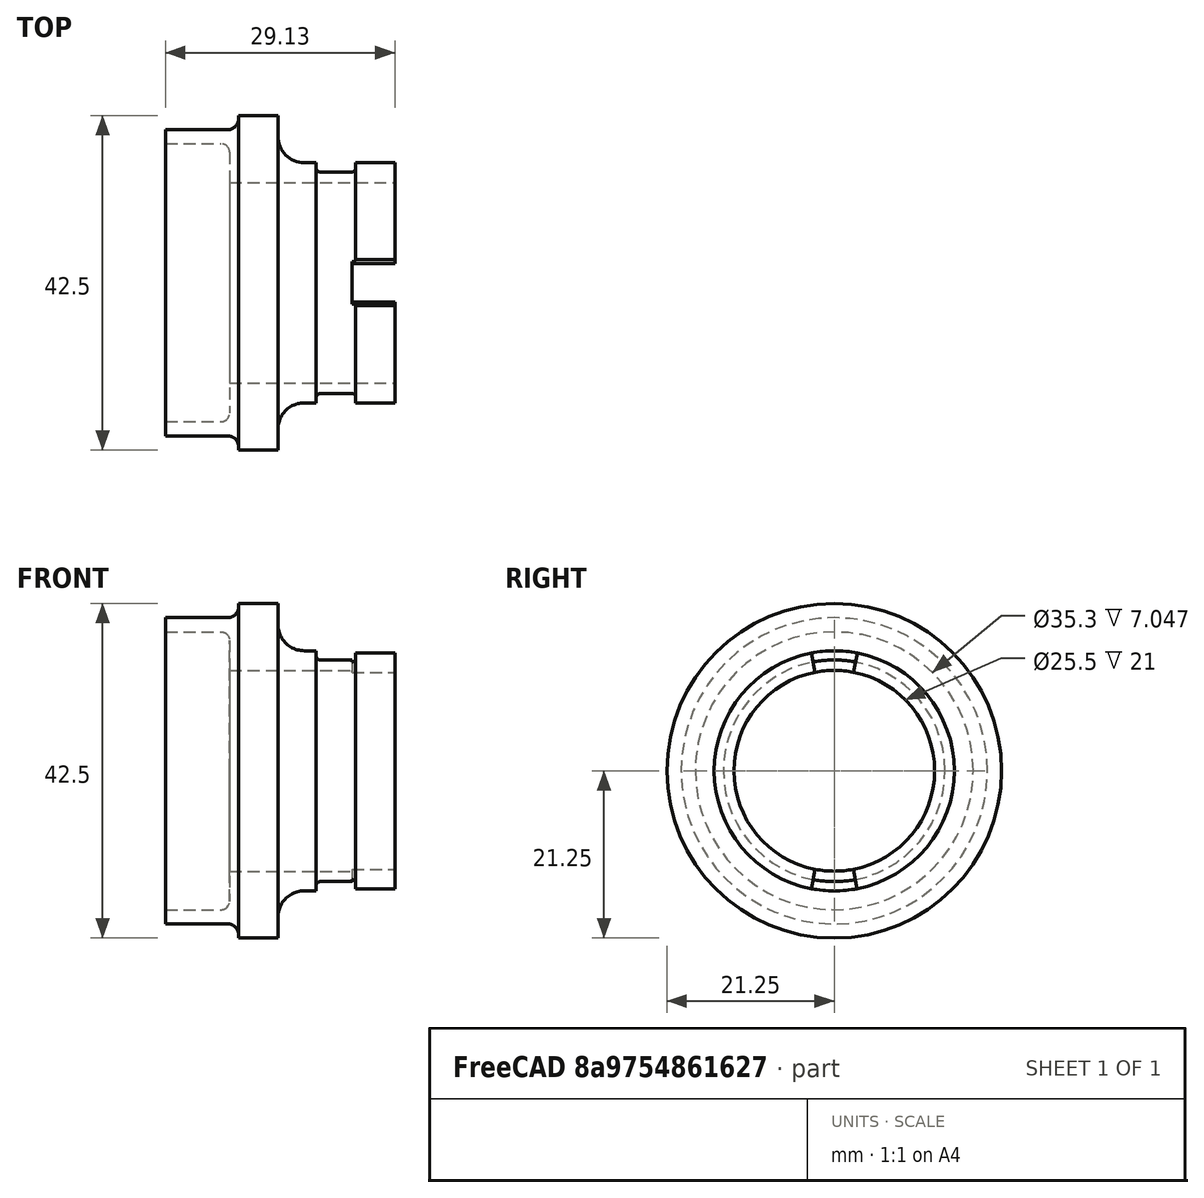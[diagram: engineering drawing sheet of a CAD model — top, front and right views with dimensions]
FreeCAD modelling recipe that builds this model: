
FCSTD DOCUMENT  (FreeCAD 0.18R16117 (Git))
Label: Adaptateur aspirateur et scie table
License: All rights reserved
LicenseURL: http://en.wikipedia.org/wiki/All_rights_reserved
objects: TechDraw::DrawViewDimension×9, Drawing::FeatureViewPart×5, TechDraw::DrawViewPart×5, Sketcher::SketchObject×4, PartDesign::Pocket×2, PartDesign::Revolution×1, PartDesign::Body×1, Drawing::FeaturePage×1, TechDraw::DrawSVGTemplate×1, TechDraw::DrawPage×1
note: 11 computed .brp shape members not serialized (recipe doc carries the construction recipe); baked Part::Feature solids carry a one-line shape summary decoded from their .brp

FEATURE [Sketcher::SketchObject] Sketch
  MapMode = 5
  Support = -> [XY_Plane]
  sketch-geometry (19):
    g0: LineSegment StartX=11.8162 StartY=18.5951 StartZ=0 EndX=11.8162 EndY=21.25 EndZ=0
    g1: LineSegment StartX=11.8162 StartY=21.25 StartZ=0 EndX=6.81623 EndY=21.25 EndZ=0
    g2: LineSegment StartX=6.81623 StartY=21.25 StartZ=0 EndX=6.81623 EndY=20.845 EndZ=0
    g3: LineSegment StartX=5.4212 StartY=19.45 StartZ=0 EndX=-2.45777 EndY=19.45 EndZ=0
    g4: LineSegment StartX=-2.45777 StartY=19.45 StartZ=0 EndX=-2.45777 EndY=17.65 EndZ=0
    g5: LineSegment StartX=-2.45777 StartY=17.65 StartZ=0 EndX=4.58894 EndY=17.65 EndZ=0
    g6: LineSegment StartX=5.67363 StartY=16.5653 StartZ=0 EndX=5.67363 EndY=12.75 EndZ=0
    g7: LineSegment StartX=5.67363 StartY=12.75 StartZ=0 EndX=26.6736 EndY=12.75 EndZ=0
    g8: LineSegment StartX=26.6736 StartY=12.75 StartZ=0 EndX=26.6736 EndY=15.25 EndZ=0
    g9: ArcOfCircle CenterX=4.58894 CenterY=16.5653 CenterZ=0 NormalX=0 NormalY=0 NormalZ=1 AngleXU=0 Radius=1.08469 StartAngle=-9e-16 EndAngle=1.5708
    g10: ArcOfCircle CenterX=5.4212 CenterY=20.845 CenterZ=0 NormalX=0 NormalY=0 NormalZ=1 AngleXU=0 Radius=1.39502 StartAngle=4.71239 EndAngle=6.28319
    g11: ArcOfCircle CenterX=15.1613 CenterY=18.5951 CenterZ=0 NormalX=0 NormalY=0 NormalZ=1 AngleXU=0 Radius=3.34505 StartAngle=3.14159 EndAngle=4.71239
    g12: LineSegment StartX=15.1613 StartY=15.25 StartZ=0 EndX=16.6736 EndY=15.25 EndZ=0
    g13: LineSegment StartX=16.6736 StartY=15.25 StartZ=0 EndX=16.6736 EndY=14.5875 EndZ=0
    g14: LineSegment StartX=17.1846 StartY=14.0765 StartZ=0 EndX=21.204 EndY=14.0765 EndZ=0
    g15: LineSegment StartX=21.6736 StartY=14.5461 StartZ=0 EndX=21.6736 EndY=15.25 EndZ=0
    g16: LineSegment StartX=21.6736 StartY=15.25 StartZ=0 EndX=26.6736 EndY=15.25 EndZ=0
    g17: ArcOfCircle CenterX=17.1846 CenterY=14.5875 CenterZ=0 NormalX=0 NormalY=0 NormalZ=1 AngleXU=0 Radius=0.510984 StartAngle=3.14159 EndAngle=4.71239
    g18: ArcOfCircle CenterX=21.204 CenterY=14.5461 CenterZ=0 NormalX=0 NormalY=0 NormalZ=1 AngleXU=0 Radius=0.469602 StartAngle=4.71239 EndAngle=6.28319
  constraints (39):
    c: Coincident(g0,g1)
    c: Coincident(g1,g2)
    c: Coincident(g3,g4)
    c: Coincident(g4,g5)
    c: Coincident(g6,g7)
    c: Coincident(g7,g8)
    c: Horizontal(g7)
    c: Horizontal(g5)
    c: Horizontal(g3)
    c: Horizontal(g1)
    c: Vertical(g4)
    c: Vertical(g2)
    c: Vertical(g6)
    c: Vertical(g8)
    c: Vertical(g0)
    c: Distance(g7,g-1) = 12.75  'Rayon intérieur côté scie'
    c: DistanceY(g8,g8) = 2.5
    c: DistanceX(g1,g1) = 5
    c: DistanceY(g-1,g4) = 17.65
    c: DistanceX(g7,g7) = 21
    c: Tangent(g5,g9) = 1.5708
    c: Tangent(g6,g9) = 1.5708
    c: Tangent(g3,g10) = 1.5708
    c: Tangent(g2,g10) = 1.5708
    c: Tangent(g0,g11) = 1.5708
    c: DistanceY(g4,g4) = 1.8
    c: Coincident(g12,g13)
    c: Coincident(g15,g16)
    c: Coincident(g16,g8)
    c: Horizontal(g16)
    c: Horizontal(g12)
    c: Horizontal(g14)
    c: Vertical(g13)
    c: Vertical(g15)
    c: DistanceX(g16,g16) = 5
    c: Tangent(g14,g17) = -1.5708
    c: Tangent(g13,g17) = -1.5708
    c: Tangent(g15,g18) = -1.5708
    c: Tangent(g14,g18) = -1.5708
FEATURE [PartDesign::Revolution] Revolution
  Angle = 360
  Axis = (1,0,0)
  Base = (0,0,0)
  Profile = -> Sketch
  ReferenceAxis = -> Sketch [H_Axis]
FEATURE [Sketcher::SketchObject] Sketch001
  MapMode = 5
  Placement = pos=(26.6736,0,0) rot=(0.57735,0.57735,0.57735;2.0944rad)
  Support = -> [Revolution]
  sketch-geometry (3):
    g0: LineSegment StartX=0 StartY=0 StartZ=0 EndX=-3 EndY=-15.4941 EndZ=0
    g1: LineSegment StartX=-3 StartY=-15.4941 StartZ=0 EndX=3 EndY=-15.4941 EndZ=0
    g2: LineSegment StartX=3 StartY=-15.4941 StartZ=0 EndX=0 EndY=0 EndZ=0
  constraints (7):
    c: Coincident(g0,g1)
    c: Coincident(g1,g2)
    c: Coincident(g2,g0)
    c: Coincident(g-1,g0)
    c: Perpendicular(g-2,g1)
    c: DistanceX(g-1,g1) = 3
    c: DistanceX(g-2,g0) = -3
FEATURE [PartDesign::Pocket] Pocket
  BaseFeature = -> Revolution
  Length = 5.45
  Length2 = 100
  Profile = -> Sketch001
  Type = 0
FEATURE [Sketcher::SketchObject] CopySketch002
  Placement = pos=(26.6736,0,0) rot=(0.57735,0.57735,0.57735;2.0944rad)
  sketch-geometry (3):
    g0: LineSegment StartX=0 StartY=0 StartZ=0 EndX=-3 EndY=15.3419 EndZ=0
    g1: LineSegment StartX=-3 StartY=15.3419 StartZ=0 EndX=3 EndY=15.3419 EndZ=0
    g2: LineSegment StartX=3 StartY=15.3419 StartZ=0 EndX=0 EndY=0 EndZ=0
  constraints (7):
    c: Coincident(g0,g1)
    c: Coincident(g1,g2)
    c: Coincident(g2,g0)
    c: Coincident(g-1,g0)
    c: Perpendicular(g-2,g1)
    c: DistanceX(g-1,g1) = 3
    c: DistanceX(g-2,g0) = -3
FEATURE [PartDesign::Pocket] Pocket001  label="Adaptateur"
  BaseFeature = -> Pocket
  Length = 5.45
  Length2 = 100
  Profile = -> CopySketch002
  Type = 0
FEATURE [PartDesign::Body] Body
  Group = -> [Sketch,Revolution,Sketch001,Pocket,Pocket001]
  Origin = -> Origin
  Tip = -> Pocket001
FEATURE [Sketcher::SketchObject] Sketch002
  MapMode = 5
  Placement = pos=(26.6736,0,0) rot=(0.57735,0.57735,0.57735;2.0944rad)
  Support = -> [Revolution]
  sketch-geometry (3):
    g0: LineSegment StartX=0 StartY=0 StartZ=0 EndX=-3 EndY=15.3419 EndZ=0
    g1: LineSegment StartX=-3 StartY=15.3419 StartZ=0 EndX=3 EndY=15.3419 EndZ=0
    g2: LineSegment StartX=3 StartY=15.3419 StartZ=0 EndX=0 EndY=0 EndZ=0
  constraints (7):
    c: Coincident(g0,g1)
    c: Coincident(g1,g2)
    c: Coincident(g2,g0)
    c: Coincident(g-1,g0)
    c: Perpendicular(g-2,g1)
    c: DistanceX(g-1,g1) = 3
    c: DistanceX(g-2,g0) = -3
FEATURE [Drawing::FeatureViewPart] Ortho  label="Cote scie"
  Direction = (1,0,0)
  HiddenWidth = 0.15
  LineWidth = 0.35
  Rotation = -90
  Scale = 1.5
  ShowHiddenLines = false
  ShowSmoothLines = false
  Source = -> Pocket001
  Tolerance = 0.05
  ViewResult = <g id="Ortho_0_0"\n   transform="rotate(-90,170,70) translate(170,70) scale(1.5,1.5)"\n  >\n<g   fill="none"\n   stroke="rgb(0, 0, 0)"\n   stroke-linecap="butt"\n   stroke-linejoin="miter"\n   stroke-width="0.233333"\n   transform="scale(1,-1)"\n  >\n<circle cx ="0" cy ="0" r ="21.25" /><path d="M14.9665 -2.9266 A15.25 15.25 0 0 1 14.9665 2.9266" /><path d="M-14.9719 2.8989 A15.25 15.25 0 0 1 -14.9719 -2.8989" /><path d="M13.8153,2.70148 C14.164,0.922951 14.164,-0.922951 13.8153,-2.70148 " /><path d="M-13.8203,-2.67591 C-14.1623,-0.913787 -14.1623,0.913787 -13.8203,2.67591 " /><path id= "6" d=" M 14.9665 -2.9266 L 12.513 -2.44683 " />\n<path d="M12.513 -2.44683 A12.75 12.75 0 0 1 12.513 2.44683" /><path id= "8" d=" M 12.513 2.44683 L 14.9665 2.9266 " />\n<path id= "9" d=" M -12.5175 2.42367 L -14.9719 2.8989 " />\n<path d="M-12.5175 2.42367 A12.75 12.75 0 0 1 -12.5175 -2.42367" /><path id= "11" d=" M -14.9719 -2.8989 L -12.5175 -2.42367 " />\n<path d="M-14.9719 -2.8989 A15.25 15.25 0 0 1 -3.73517e-15 -15.25" /><path d="M0 -15.25 A15.25 15.25 0 0 1 14.9665 -2.9266" /><path d="M0 -12.75 A12.75 12.75 0 0 1 12.513 -2.44683" /><path d="M-12.5175 -2.42367 A12.75 12.75 0 0 1 -3.12285e-15 -12.75" /><path d="M12.513 2.44683 A12.75 12.75 0 0 1 -12.5175 2.42367" /><path d="M14.9665 2.9266 A15.25 15.25 0 0 1 -14.9719 2.8989" /></g>\n</g>
  Visible = true
  X = 170
  Y = 70
FEATURE [Drawing::FeatureViewPart] Ortho001  label="Vue angle"
  Direction = (0.57735,0.57735,0.57735)
  HiddenWidth = 0.15
  LineWidth = 0.35
  Rotation = 120
  Scale = 2.25
  ShowHiddenLines = false
  ShowSmoothLines = false
  Source = -> Pocket001
  Tolerance = 0.05
  ViewResult = <blob: 4174 chars omitted>
  Visible = true
  X = 330
  Y = 75
FEATURE [Drawing::FeatureViewPart] Ortho002  label="Dessus avec rainure"
  Direction = (0,1,0)
  HiddenWidth = 0.15
  LineWidth = 0.35
  Rotation = 0
  Scale = 1.5
  ShowHiddenLines = false
  ShowSmoothLines = false
  Source = -> Pocket001
  Tolerance = 0.05
  ViewResult = <blob: 5895 chars omitted>
  Visible = true
  X = 75
  Y = 240
FEATURE [Drawing::FeatureViewPart] Ortho003  label="Cote aspi"
  Direction = (-1,0,0)
  HiddenWidth = 0.15
  LineWidth = 0.35
  Rotation = -90
  Scale = 1.5
  ShowHiddenLines = false
  ShowSmoothLines = false
  Source = -> Pocket001
  Tolerance = 0.05
  ViewResult = <g id="Ortho_0_2"\n   transform="rotate(-90,76.02,70) translate(76.02,70) scale(1.5,1.5)"\n  >\n<g   fill="none"\n   stroke="rgb(0, 0, 0)"\n   stroke-linecap="butt"\n   stroke-linejoin="miter"\n   stroke-width="0.233333"\n   transform="scale(1,-1)"\n  >\n<circle cx ="0" cy ="0" r ="21.25" /><circle cx ="0" cy ="0" r ="19.45" /><circle cx ="0" cy ="0" r ="17.65" /><circle cx ="0" cy ="0" r ="12.75" /></g>\n</g>
  Visible = true
  X = 76.02
  Y = 70
FEATURE [Drawing::FeatureViewPart] Ortho005  label="Dessus avec pocket"
  Direction = (0,0,1)
  HiddenWidth = 0.15
  LineWidth = 0.35
  Rotation = 90
  Scale = 1.5
  ShowHiddenLines = false
  ShowSmoothLines = false
  Source = -> Pocket001
  Tolerance = 0.05
  ViewResult = <blob: 5137 chars omitted>
  Visible = true
  X = 76.022
  Y = 130.338
FEATURE [Drawing::FeaturePage] Page
  EditableTexts = AUTHOR NAME | CREATION DATE | SUPERVISOR NAME | CHECK DATE | SCALE | WEIGHT | NUMBER | SHEET | TITLE | SUBTITLE
  Group = -> [Ortho,Ortho001,Ortho002,Ortho003,Ortho005]
  Template = C:/Program Files/FreeCAD 0.18/data/Mod/Drawing/Templates/A3_Landscape.svg
FEATURE [TechDraw::DrawSVGTemplate] Template
  EditableTexts = Designed_by_Name=R. BELLO; Drawing_number=#00-001; FC-Date=30/09/2019; FC-SC=?; FC-SH=Sheet; FC-Title=Adaptateur aspirateur; Subtitle=Scie table Peugeot / aspirateur Parkside; Weight=31 g
  Height = 210
  Orientation = 1
  Width = 297
FEATURE [TechDraw::DrawViewPart] View001  label="Côté scie table"
  Caption = Côté scie table
  CoarseView = false
  Direction = (1,0,0)
  Focus = 100
  HardHidden = false
  IsoCount = 0
  IsoHidden = false
  IsoVisible = false
  LockPosition = false
  Perspective = false
  Rotation = 0
  ScaleType = 0
  SeamHidden = false
  SeamVisible = false
  SmoothHidden = false
  SmoothVisible = false
  Source = -> [Pocket001]
  X = 161.011
  Y = 167.786
FEATURE [TechDraw::DrawViewPart] View  label="Projeté"
  CoarseView = false
  Direction = (0.5,-0.5,0.707)
  Focus = 100
  HardHidden = false
  IsoCount = -3
  IsoHidden = false
  IsoVisible = false
  LockPosition = false
  Perspective = false
  Rotation = 0
  Scale = 2
  ScaleType = 0
  SeamHidden = false
  SeamVisible = false
  SmoothHidden = false
  SmoothVisible = false
  Source = -> [Pocket001]
  X = 65.3418
  Y = 138.795
FEATURE [TechDraw::DrawViewPart] View002  label="Profile"
  CoarseView = false
  Direction = (0,1,0)
  Focus = 100
  HardHidden = false
  IsoCount = 0
  IsoHidden = false
  IsoVisible = false
  LockPosition = false
  Perspective = false
  Rotation = 0
  Scale = 1.5
  ScaleType = 0
  SeamHidden = false
  SeamVisible = false
  SmoothHidden = false
  SmoothVisible = false
  Source = -> [Pocket001]
  X = 244.135
  Y = 129.962
FEATURE [TechDraw::DrawViewDimension] Dimension
  Arbitrary = false
  FormatSpec = %.2f
  LockPosition = false
  MeasureType = 1
  OverTolerance = 0
  References2D = -> [View002]
  Rotation = 0
  ScaleType = 0
  Type = 1
  UnderTolerance = 0
  X = -3.08826
  Y = -45.5863
FEATURE [TechDraw::DrawViewDimension] Dimension001
  Arbitrary = false
  FormatSpec = %.2f
  LockPosition = false
  MeasureType = 1
  OverTolerance = 0
  References2D = -> [View002]
  Rotation = 0
  ScaleType = 0
  Type = 1
  UnderTolerance = 0
  X = 3.16636
  Y = 52.3495
FEATURE [TechDraw::DrawViewDimension] Dimension002
  Arbitrary = false
  FormatSpec = %.2f
  LockPosition = false
  MeasureType = 1
  OverTolerance = 0
  References2D = -> [View002]
  Rotation = 0
  ScaleType = 0
  Type = 2
  UnderTolerance = 0
  X = -37.0471
  Y = -0.184978
FEATURE [TechDraw::DrawViewDimension] Dimension003
  Arbitrary = false
  FormatSpec = %.2f
  LockPosition = false
  MeasureType = 1
  OverTolerance = 0
  References2D = -> [View002]
  Rotation = 0
  ScaleType = 0
  Type = 2
  UnderTolerance = 0
  X = 27.2766
  Y = 0.723739
FEATURE [TechDraw::DrawViewPart] View003  label="Coté aspirateur"
  Caption = Coté aspirateur
  CoarseView = false
  Direction = (-1,0,0)
  Focus = 100
  HardHidden = false
  IsoCount = 0
  IsoHidden = false
  IsoVisible = false
  LockPosition = false
  Perspective = false
  Rotation = 0
  ScaleType = 0
  SeamHidden = false
  SeamVisible = false
  SmoothHidden = false
  SmoothVisible = false
  Source = -> [Pocket001]
  X = 161.776
  Y = 105.561
FEATURE [TechDraw::DrawViewDimension] Dimension004
  Arbitrary = false
  FormatSpec = %.2f
  LockPosition = false
  MeasureType = 1
  OverTolerance = 0
  References2D = -> [View001]
  Rotation = 0
  ScaleType = 0
  Type = 2
  UnderTolerance = 0
  X = -34.0704
  Y = -0.002695
FEATURE [TechDraw::DrawViewDimension] Dimension005
  Arbitrary = false
  FormatSpec = %.2f
  LockPosition = false
  MeasureType = 1
  OverTolerance = 0
  References2D = -> [View001]
  Rotation = 0
  ScaleType = 0
  Type = 2
  UnderTolerance = 0
  X = 29.3583
  Y = -0.219375
FEATURE [TechDraw::DrawViewPart] View004
  Caption = Encoche
  CoarseView = false
  Direction = (0,0,0.01)
  Focus = 100
  HardHidden = false
  IsoCount = 0
  IsoHidden = false
  IsoVisible = false
  LockPosition = false
  Perspective = false
  Rotation = 0
  ScaleType = 0
  SeamHidden = false
  SeamVisible = false
  SmoothHidden = false
  SmoothVisible = false
  Source = -> [Pocket001]
  X = 49.5955
  Y = 51.9501
FEATURE [TechDraw::DrawViewDimension] Dimension007
  Arbitrary = false
  FormatSpec = %.2f
  LockPosition = false
  MeasureType = 1
  OverTolerance = 0
  References2D = -> [View004]
  Rotation = 0
  ScaleType = 0
  Type = 2
  UnderTolerance = 0
  X = 25.1484
  Y = 16.4795
FEATURE [TechDraw::DrawViewDimension] Dimension008
  Arbitrary = false
  FormatSpec = %.2f
  LockPosition = false
  MeasureType = 1
  OverTolerance = 0
  References2D = -> [View004]
  Rotation = 0
  ScaleType = 0
  Type = 1
  UnderTolerance = 0
  X = -11.0278
  Y = 32.3383
FEATURE [TechDraw::DrawViewDimension] Dimension009
  Arbitrary = false
  FormatSpec = ⌀%.2f
  LockPosition = false
  MeasureType = 1
  OverTolerance = 0
  References2D = -> [View003]
  Rotation = 0
  ScaleType = 0
  Type = 5
  UnderTolerance = 0
  X = 36.3377
  Y = -20.5059
FEATURE [TechDraw::DrawPage] Page001
  KeepUpdated = true
  ProjectionType = 0
  Template = -> Template
  Views = -> [View,View001,View002,Dimension,Dimension001,Dimension002,Dimension003,View003,Dimension004,Dimension005,View004,Dimension007,Dimension008,Dimension009]
